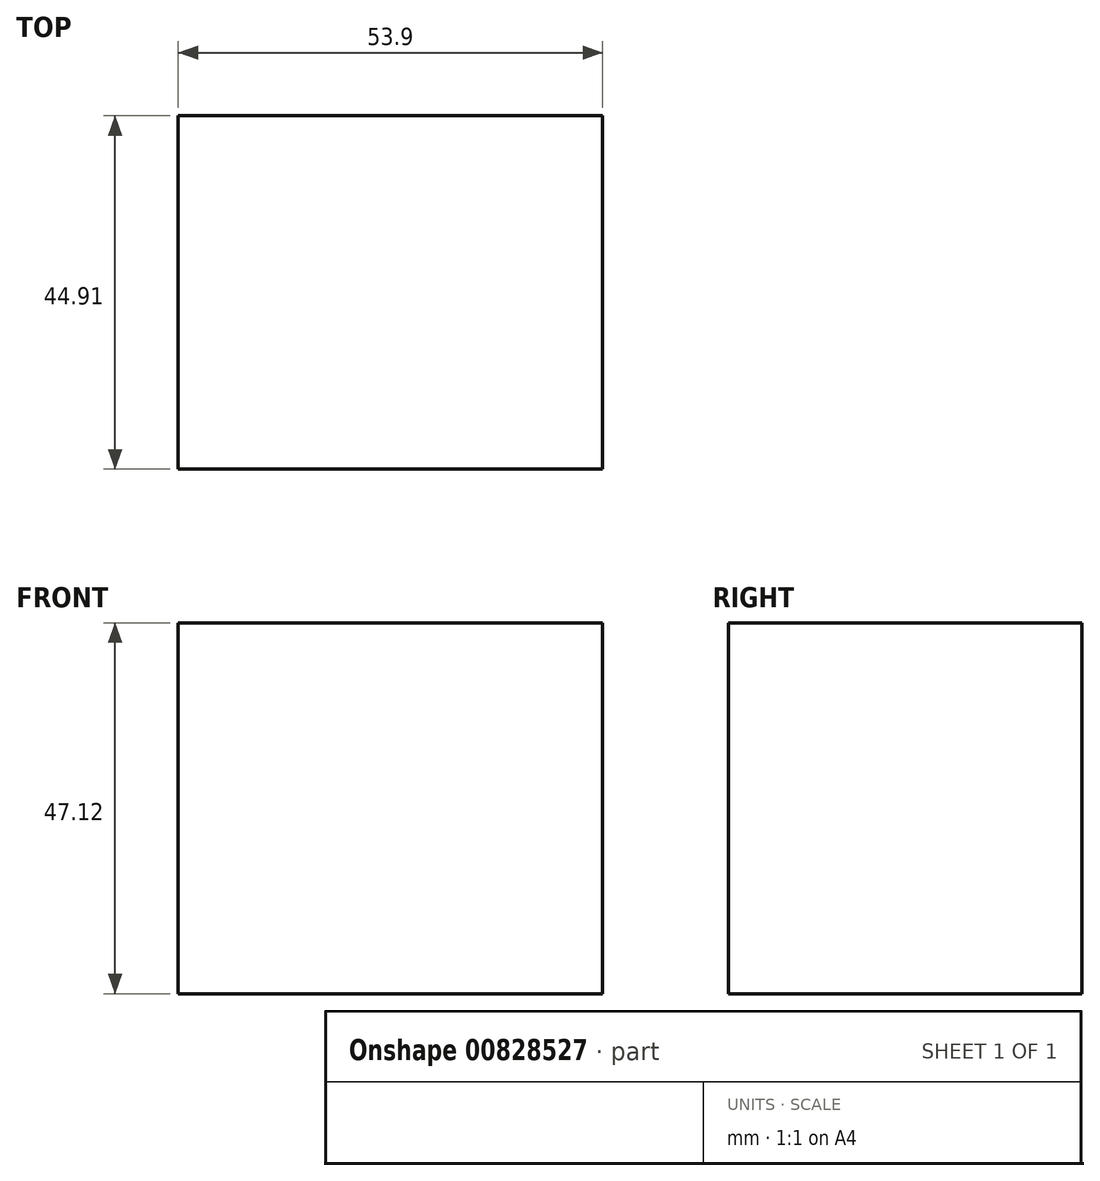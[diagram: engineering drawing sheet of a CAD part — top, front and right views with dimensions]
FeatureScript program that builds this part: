
annotation { "Feature Type Name" : "Feature", "Feature Type Description" : "" }
export const myFeature = defineFeature(function(context is Context, id is Id, definition is map)
    precondition{}
    {
        {
            var Q0;
            Q0=qCreatedBy(makeId("Front.planeOp"),FACE);
            var sketch = newSketch(context, id + "F0", { "sketchPlane" : qUnion([Q0])});
            skLineSegment(sketch, "E0.bottom", {"start": v(0, 63.85) * mm, "end": v(53.9, 63.85) * mm});
            skLineSegment(sketch, "E0.top", {"start": v(0, 16.73) * mm, "end": v(53.9, 16.73) * mm});
            skLineSegment(sketch, "E0.left", {"start": v(0, 63.85) * mm, "end": v(0, 16.73) * mm});
            skLineSegment(sketch, "E0.right", {"start": v(53.9, 63.85) * mm, "end": v(53.9, 16.73) * mm});
            skSolve(sketch);
        }
        {
            var Q0;
            Q0 = qSketchRegion(id + "F0", true);
            extrude(context, id + "F1", {"entities" : qUnion([Q0]), "depth" : 44.9 * mm, "offsetDistance" : 25.4 * mm});
        }
    });
